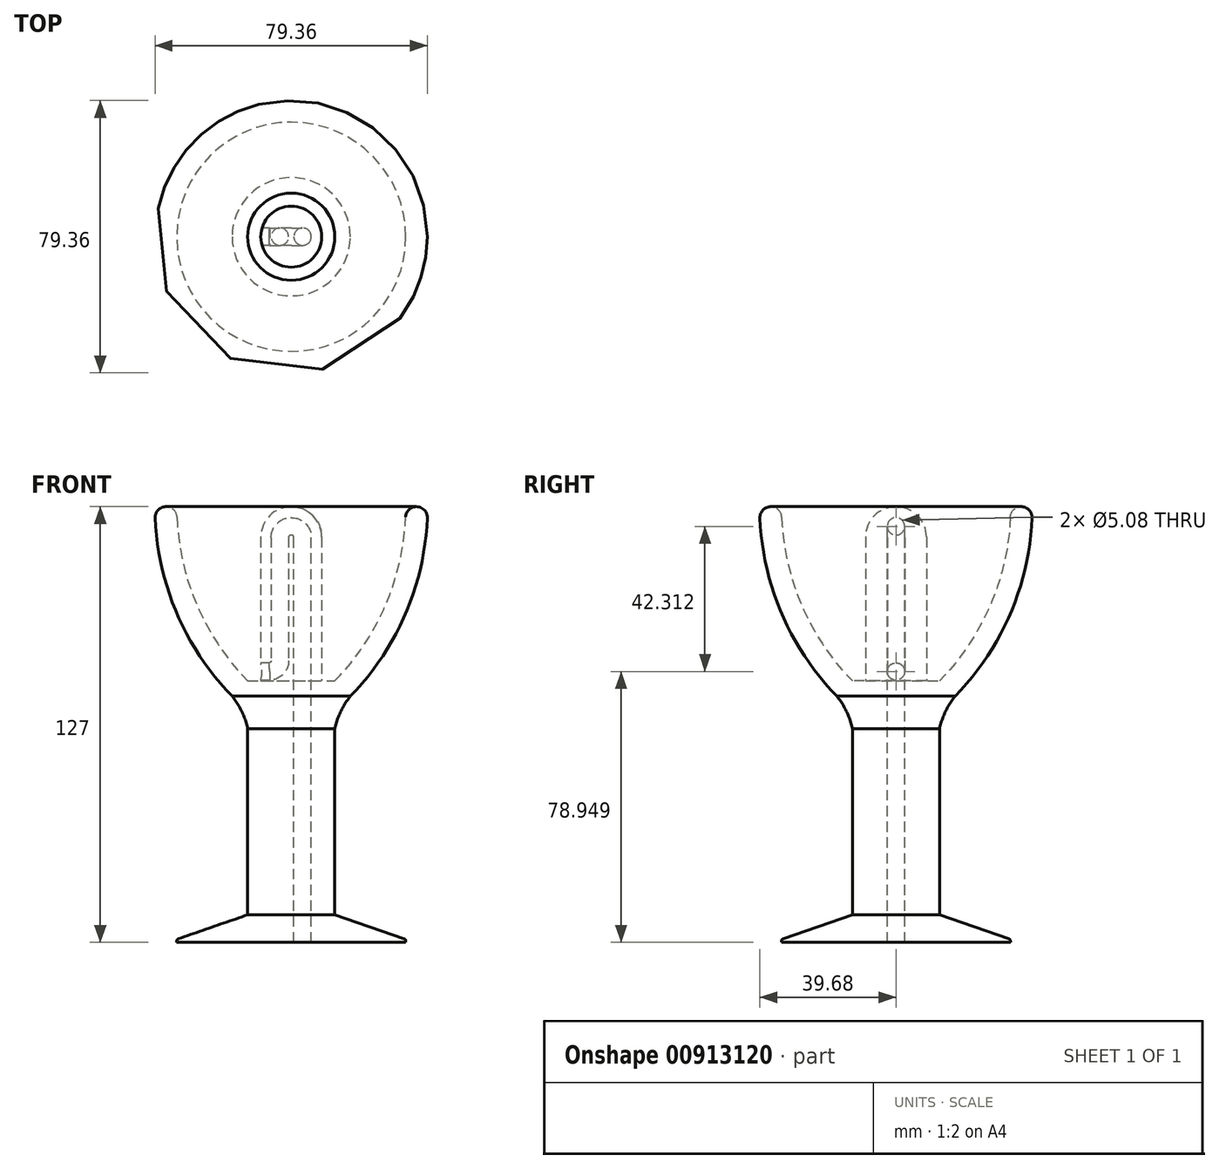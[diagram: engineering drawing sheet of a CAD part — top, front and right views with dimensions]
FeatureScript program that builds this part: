
annotation { "Feature Type Name" : "Feature", "Feature Type Description" : "" }
export const myFeature = defineFeature(function(context is Context, id is Id, definition is map)
    precondition{}
    {
        {
            var Q0;
            Q0=qCreatedBy(makeId("Front.planeOp"),FACE);
            var sketch = newSketch(context, id + "F0", { "sketchPlane" : qUnion([Q0])});
            skLineSegment(sketch, "E0.bottom", {"start": v(0, 0) * mm, "end": v(12.7, 0) * mm});
            skLineSegment(sketch, "E0.top", {"start": v(6.35, 76.2) * mm, "end": v(12.7, 76.2) * mm});
            skLineSegment(sketch, "E0.left", {"start": v(0, 0) * mm, "end": v(0, 76.2) * mm});
            skLineSegment(sketch, "E0.right", {"start": v(12.7, 8.05) * mm, "end": v(12.7, 62.23) * mm});
            skLineSegment(sketch, "E1", {"start": v(12.7, 8.05) * mm, "end": v(32.9, 1.08) * mm});
            skLineSegment(sketch, "E2", {"start": v(33.4, 0.37) * mm, "end": v(33.4, 0) * mm});
            skLineSegment(sketch, "E3", {"start": v(33.4, 0) * mm, "end": v(12.7, 0) * mm});
            skPoint(sketch, "E4.visualSharp", {"position": v(33.4, 0.9) * mm});
            skArc(sketch, "E4.filletArc", {"start": v(33.4, 0.37) * mm, "mid": v(33.26, 0.8) * mm, "end": v(32.9, 1.08) * mm});
            skLineSegment(sketch, "E5", {"start": v(33.4, 0) * mm, "end": v(33.4, 0.9) * mm, "construction": true});
            skArc(sketch, "E6", {"start": v(12.7, 76.2) * mm, "mid": v(28.02, 99.57) * mm, "end": v(33.4, 127) * mm});
            skArc(sketch, "E7.0", {"start": v(17.24, 71.76) * mm, "mid": v(33.9, 97.18) * mm, "end": v(39.75, 127) * mm});
            skArc(sketch, "E8", {"start": v(17.24, 71.76) * mm, "mid": v(14.41, 67.26) * mm, "end": v(12.7, 62.23) * mm});
            skLineSegment(sketch, "E9", {"start": v(33.4, 127) * mm, "end": v(39.75, 127) * mm});
            skLineSegment(sketch, "E10", {"start": v(0, 127) * mm, "end": v(6.35, 127) * mm, "construction": true});
            skLineSegment(sketch, "E11.left", {"start": v(0, 76.2) * mm, "end": v(0, 127) * mm});
            skLineSegment(sketch, "E12", {"start": v(0, 127) * mm, "end": v(0, 127) * mm});
            skPoint(sketch, "E13.visualSharp", {"position": v(6.35, 127) * mm});
            skPoint(sketch, "E14.end.orphan", {"position": v(6.35, 0) * mm});
            skArc(sketch, "E15.0", {"start": v(8.9, 118.1) * mm, "mid": v(6.29, 124.4) * mm, "end": v(0, 127) * mm});
            skLineSegment(sketch, "E15.1", {"start": v(8.9, 76.2) * mm, "end": v(8.9, 118.1) * mm});
            skSolve(sketch);
        }
        {
            var Q0;
            Q0=makeQuery(id+"F0.imprint","IMPRINT",FACE,{"disambiguationData":[TD([[makeQuery(id+"F0.imprint","IMPRINT",EDGE,{"derivedFrom":sQuery(id+"F0.wireOp",EDGE,"E0.bottom")}),1.0]])]});
            var Q1;
            Q1=sQuery(id+"F0.wireOp",EDGE,"E0.left");
            revolve(context, id + "F1", {"surfaceOperationType" : NewSurfaceOperationType.NEW, "entities" : qUnion([Q0]), "axis" : qUnion([Q1]), "revolveType" : RevolveType.FULL});
        }
        {
            var Q0;
            Q0=qCreatedBy(makeId("Front.planeOp"),FACE);
            var sketch = newSketch(context, id + "F2", { "sketchPlane" : qUnion([Q0])});
            skArc(sketch, "E16.0", {"start": v(3.3, 118.08) * mm, "mid": v(2.37, 120.33) * mm, "end": v(0.13, 121.26) * mm});
            skLineSegment(sketch, "E16.1", {"start": v(3.3, 76.2) * mm, "end": v(3.3, 118.08) * mm});
            skLineSegment(sketch, "E17.MirrorCS", {"start": v(-3.3, 82.12) * mm, "end": v(-3.3, 118.08) * mm});
            skArc(sketch, "E18.MirrorCS", {"start": v(-3.3, 118.08) * mm, "mid": v(-2.37, 120.33) * mm, "end": v(-0.13, 121.26) * mm});
            skLineSegment(sketch, "E19", {"start": v(3.3, 76.2) * mm, "end": v(3.3, 0) * mm});
            skArc(sketch, "E20", {"start": v(-6.32, 78.95) * mm, "mid": v(-4.18, 79.93) * mm, "end": v(-3.3, 82.12) * mm});
            skPoint(sketch, "E21.orphan", {"position": v(-3.3, 76.2) * mm});
            skLineSegment(sketch, "E22", {"start": v(0.13, 121.26) * mm, "end": v(-0.13, 121.26) * mm});
            skLineSegment(sketch, "E23", {"start": v(-6.32, 78.95) * mm, "end": v(-7.78, 78.95) * mm});
            skLineSegment(sketch, "E24", {"start": v(-7.78, 78.95) * mm, "end": v(-9.82, 78.95) * mm});
            skPoint(sketch, "E25.orphan", {"position": v(-3.3, 120.65) * mm});
            skPoint(sketch, "E26.orphan", {"position": v(3.3, 120.65) * mm});
            skSolve(sketch);
        }
        {
            var Q0;
            Q0=makeQuery(id+"F1.opRevolve","SWEPT_FACE",FACE,{"disambiguationData":[OSD([sQuery(id+"F0.wireOp",EDGE,"E0.bottom"),sQuery(id+"F0.wireOp",EDGE,"E3")])]});
            var sketch = newSketch(context, id + "F3", { "sketchPlane" : qUnion([Q0])});
            skCircle(sketch, "E27", {"center": v(3.3, 0) * mm, "radius": 2.54 * mm});
            skSolve(sketch);
        }
        {
            var Q0;
            Q0=makeQuery(id+"F3.imprint","IMPRINT",FACE,{"disambiguationData":[TD([[makeQuery(id+"F3.imprint","IMPRINT",EDGE,{"derivedFrom":sQuery(id+"F3.wireOp",EDGE,"E27")}),1.0]])]});
            var Q1;
            Q1=sQuery(id+"F2.wireOp",EDGE,"E19");
            var Q2;
            Q2=sQuery(id+"F2.wireOp",EDGE,"E16.1");
            var Q3;
            Q3=sQuery(id+"F2.wireOp",EDGE,"E16.0");
            var Q4;
            Q4=sQuery(id+"F2.wireOp",EDGE,"E22");
            var Q5;
            Q5=sQuery(id+"F2.wireOp",EDGE,"E18.MirrorCS");
            var Q6;
            Q6=sQuery(id+"F2.wireOp",EDGE,"E17.MirrorCS");
            var Q7;
            Q7=sQuery(id+"F2.wireOp",EDGE,"E20");
            var Q8;
            Q8=sQuery(id+"F2.wireOp",EDGE,"E23");
            var Q9;
            Q9=sQuery(id+"F2.wireOp",EDGE,"E24");
            sweep(context, id + "F4", {"operationType" : NewBodyOperationType.REMOVE, "profiles" : qUnion([Q0]), "path" : qUnion([Q1, Q2, Q3, Q4, Q5, Q6, Q7, Q8, Q9])});
        }
        {
            var Q0;
            Q0=makeQuery(id+"F1.opRevolve","SWEPT_EDGE",EDGE,{"disambiguationData":[OSD([sQuery(id+"F0.wireOp",EDGE,"E6"),sQuery(id+"F0.wireOp",EDGE,"E9")])]});
            var Q1;
            Q1=makeQuery(id+"F1.opRevolve","SWEPT_EDGE",EDGE,{"disambiguationData":[OSD([sQuery(id+"F0.wireOp",EDGE,"E7.0"),sQuery(id+"F0.wireOp",EDGE,"E9")])]});
            fillet(context, id + "F5", {"entities" : qUnion([Q0, Q1]), "radius" : 3.17 * mm, "tangentPropagation" : true, "allowEdgeOverflow" : false});
        }
    });
